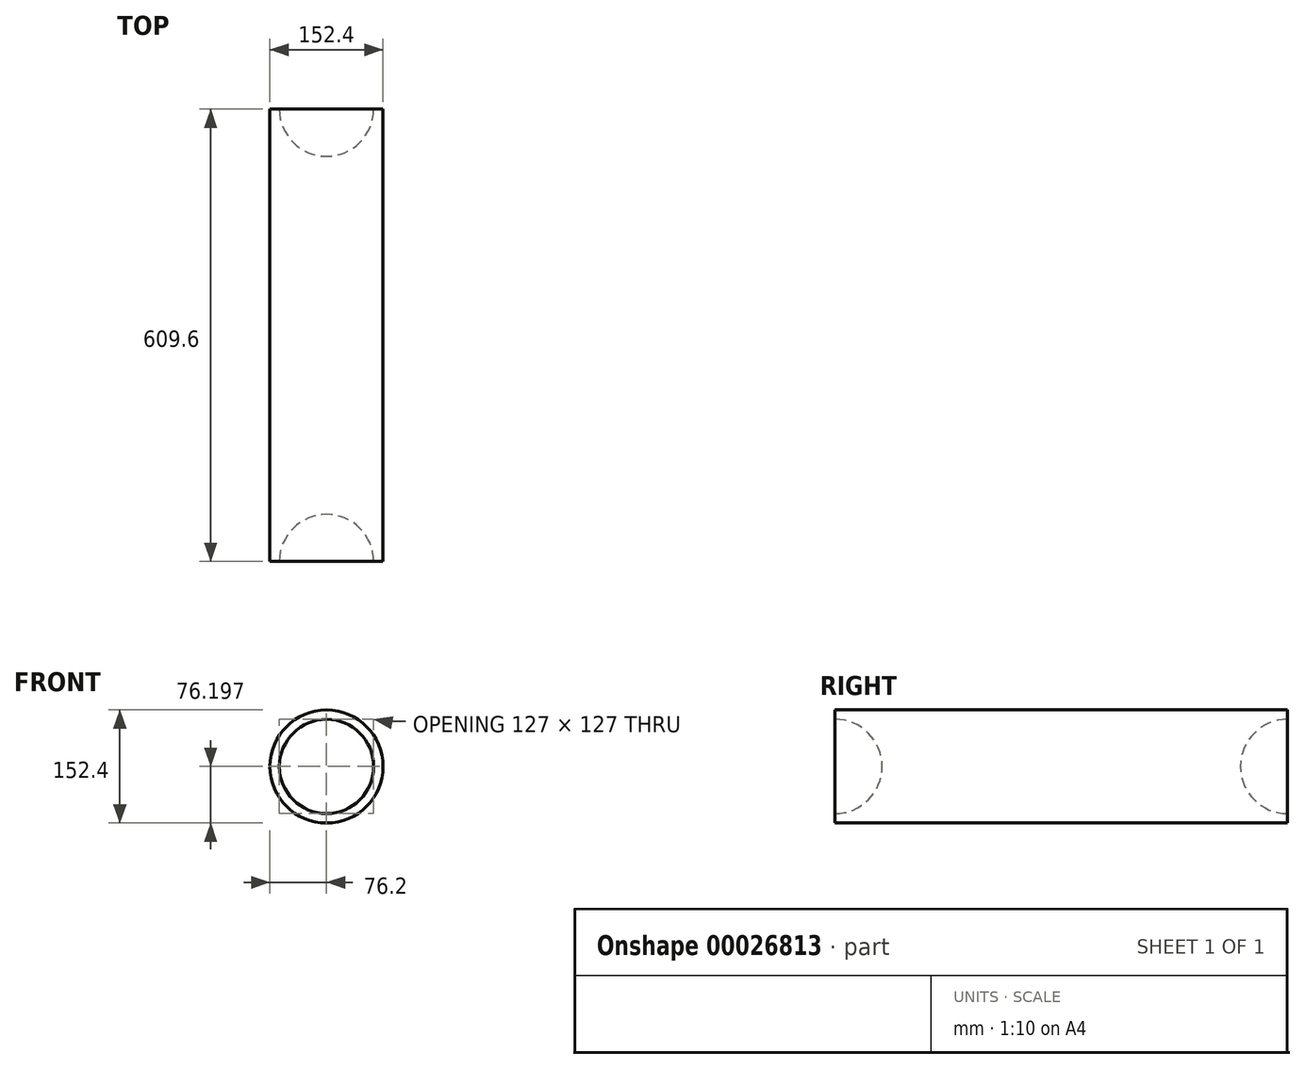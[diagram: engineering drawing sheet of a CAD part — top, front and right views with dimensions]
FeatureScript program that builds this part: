
annotation { "Feature Type Name" : "Feature", "Feature Type Description" : "" }
export const myFeature = defineFeature(function(context is Context, id is Id, definition is map)
    precondition{}
    {
        {
            var Q0;
            Q0=qCreatedBy(makeId("Front.planeOp"),FACE);
            var sketch = newSketch(context, id + "F0", { "sketchPlane" : qUnion([Q0])});
            skCircle(sketch, "E0", {"center": v(-4.47, 3.43) * mm, "radius": 76.2 * mm});
            skSolve(sketch);
        }
        {
            var Q0;
            Q0=makeQuery(id+"F0.imprint","IMPRINT",FACE,{"disambiguationData":[TD([[makeQuery(id+"F0.imprint","IMPRINT",EDGE,{"derivedFrom":sQuery(id+"F0.wireOp",EDGE,"E0")}),1.0]])]});
            extrude(context, id + "F1", {"entities" : qUnion([Q0]), "depth" : 609.6 * mm});
        }
        {
            var Q0;
            Q0=makeQuery(id+"F1.opExtrude","CAP_FACE",FACE,{"disambiguationData":[OSD([sQuery(id+"F0.wireOp",EDGE,"E0")])],"isStart":false});
            var sketch = newSketch(context, id + "F2", { "sketchPlane" : qUnion([Q0])});
            skArc(sketch, "E1", {"start": v(-4.47, 66.93) * mm, "mid": v(-67.97, 3.43) * mm, "end": v(-4.47, -60.07) * mm});
            skLineSegment(sketch, "E2", {"start": v(-4.47, -60.07) * mm, "end": v(-4.47, 66.93) * mm});
            skSolve(sketch);
        }
        {
            var Q0;
            Q0=makeQuery(id+"F2.imprint","IMPRINT",FACE,{"disambiguationData":[TD([[makeQuery(id+"F2.imprint","IMPRINT",EDGE,{"derivedFrom":sQuery(id+"F2.wireOp",EDGE,"E1")}),1.0]])]});
            var Q1;
            Q1=sQuery(id+"F2.wireOp",EDGE,"E2");
            revolve(context, id + "F3", {"operationType" : NewBodyOperationType.REMOVE, "entities" : qUnion([Q0]), "axis" : qUnion([Q1]), "revolveType" : RevolveType.ONE_DIRECTION, "oppositeDirection" : true, "angle" : 180 * degree});
        }
        {
            var Q0;
            Q0=makeQuery(id+"F1.opExtrude","CAP_FACE",FACE,{"disambiguationData":[OSD([sQuery(id+"F0.wireOp",EDGE,"E0")])],"isStart":true});
            var sketch = newSketch(context, id + "F4", { "sketchPlane" : qUnion([Q0])});
            skArc(sketch, "E3", {"start": v(4.47, 66.93) * mm, "mid": v(-59.03, 3.43) * mm, "end": v(4.47, -60.07) * mm});
            skLineSegment(sketch, "E4", {"start": v(4.47, -60.07) * mm, "end": v(4.47, 66.93) * mm});
            skSolve(sketch);
        }
        {
            var Q0;
            Q0=makeQuery(id+"F4.imprint","IMPRINT",FACE,{"disambiguationData":[TD([[makeQuery(id+"F4.imprint","IMPRINT",EDGE,{"derivedFrom":sQuery(id+"F4.wireOp",EDGE,"E3")}),1.0]])]});
            var Q1;
            Q1=sQuery(id+"F4.wireOp",EDGE,"E4");
            revolve(context, id + "F5", {"operationType" : NewBodyOperationType.REMOVE, "entities" : qUnion([Q0]), "axis" : qUnion([Q1]), "revolveType" : RevolveType.ONE_DIRECTION, "oppositeDirection" : true, "angle" : 180 * degree});
        }
    });
